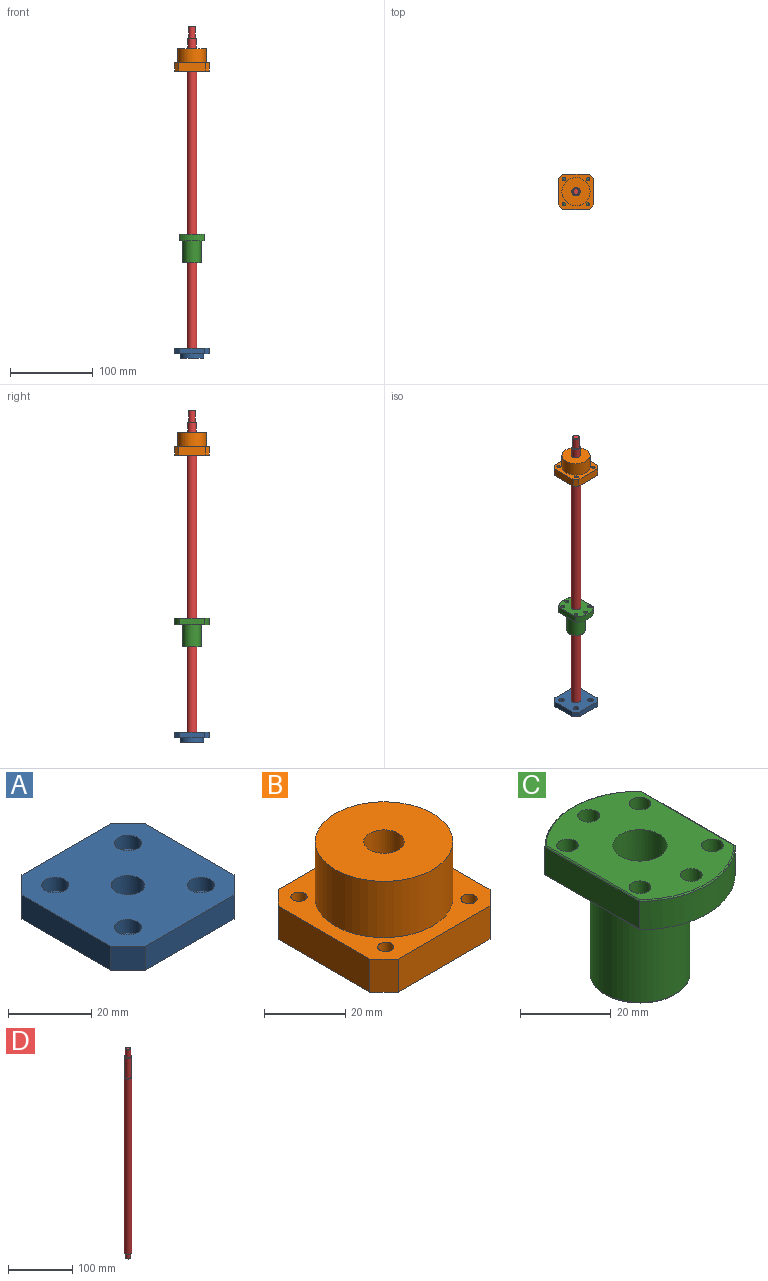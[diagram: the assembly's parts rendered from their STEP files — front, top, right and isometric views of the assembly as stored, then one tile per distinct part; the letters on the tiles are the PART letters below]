
ASSEMBLY  parts=4 mates=3
PART A: 25 faces, bbox 42x42x12 mm
  f0: cylinder r=2mm len=4mm, axis (0,0,-1), area 37.7mm2, adj f9,f23
  f1: cylinder r=2mm len=4mm, axis (0,0,-1), area 37.7mm2, adj f9,f21
  f2: cylinder r=2mm len=4mm, axis (0,0,-1), area 37.7mm2, adj f9,f19
  f3: cylinder r=2mm len=4mm, axis (0,0,-1), area 37.7mm2, adj f9,f17
  f4: plane 30x7mm, normal (0,-1,0), area 210mm2, adj f9,f10,f15,f16
  f5: plane 30x7mm, normal (1,0,0), area 210mm2, adj f9,f10,f14,f15
  f6: plane 30x7mm, normal (0,1,0), area 210mm2, adj f9,f10,f13,f14
  f7: cylinder r=4mm len=12mm, axis (0,0,1), area 301.6mm2, adj f10,f12
  f8: plane 30x7mm, normal (-1,0,0), area 210mm2, adj f9,f10,f13,f16
  f9: plane 42x42mm, normal (0,0,-1), area 1026mm2, adj f0,f1,f2,f3,f4,f5,f6,f8
  f10: plane 42x42mm, normal (0,0,1), area 1509mm2, adj f4,f5,f6,f7,f8,f13,f14,f15
  f11: cylinder r=14mm len=28mm, axis (0,0,1), area 439.8mm2, adj f9,f12
  f12: plane 28x28mm, normal (0,0,-1), area 565.5mm2, adj f7,f11
  f13: plane 7x6mm, normal (-0.71,0.71,0), area 59.4mm2, adj f6,f8,f9,f10
  f14: plane 7x6mm, normal (0.71,0.71,0), area 59.4mm2, adj f5,f6,f9,f10
  f15: plane 7x6mm, normal (0.71,-0.71,0), area 59.4mm2, adj f4,f5,f9,f10
  f16: plane 7x6mm, normal (-0.71,-0.71,0), area 59.4mm2, adj f4,f8,f9,f10
  f17: plane 6.5x6.5mm, normal (0,0,1), area 20.6mm2, adj f3,f18
  f18: cylinder r=3.25mm len=6.5mm, axis (0,0,1), area 81.7mm2, adj f10,f17
  f19: plane 6.5x6.5mm, normal (0,0,1), area 20.6mm2, adj f2,f20
  f20: cylinder r=3.25mm len=6.5mm, axis (0,0,1), area 81.7mm2, adj f10,f19
  f21: plane 6.5x6.5mm, normal (0,0,1), area 20.6mm2, adj f1,f22
  f22: cylinder r=3.25mm len=6.5mm, axis (0,0,1), area 81.7mm2, adj f10,f21
  f23: plane 6.5x6.5mm, normal (0,0,1), area 20.6mm2, adj f0,f24
  f24: cylinder r=3.25mm len=6.5mm, axis (0,0,1), area 81.7mm2, adj f10,f23
PART B: 25 faces, bbox 42x42x27 mm
  f0: cylinder r=2mm len=4mm, axis (0,0,1), area 50.3mm2, adj f8,f22
  f1: cylinder r=2mm len=4mm, axis (0,0,1), area 50.3mm2, adj f8,f20
  f2: cylinder r=2mm len=4mm, axis (0,0,1), area 50.3mm2, adj f8,f18
  f3: cylinder r=2mm len=4mm, axis (0,0,1), area 50.3mm2, adj f8,f16
  f4: plane 32x10mm, normal (1,0,0), area 320mm2, adj f8,f9,f13,f15
  f5: plane 32x10mm, normal (0,1,0), area 320mm2, adj f8,f9,f14,f15
  f6: plane 32x10mm, normal (-1,0,0), area 320mm2, adj f8,f9,f12,f14
  f7: plane 32x10mm, normal (0,-1,0), area 320mm2, adj f8,f9,f12,f13
  f8: plane 42x42mm, normal (0,0,1), area 755.8mm2, adj f0,f1,f2,f3,f4,f5,f6,f7
  f9: plane 42x42mm, normal (0,0,-1), area 1434.4mm2, adj f4,f5,f6,f7,f12,f13,f14,f15
  f10: cylinder r=17mm len=34mm, axis (0,0,-1), area 1815.8mm2, adj f8,f11
  f11: plane 34x34mm, normal (0,0,1), area 829.4mm2, adj f10,f24
  f12: plane 10x5mm, normal (-0.71,-0.71,0), area 70.7mm2, adj f6,f7,f8,f9
  f13: plane 10x5mm, normal (0.71,-0.71,0), area 70.7mm2, adj f4,f7,f8,f9
  f14: plane 10x5mm, normal (-0.71,0.71,0), area 70.7mm2, adj f5,f6,f8,f9
  f15: plane 10x5mm, normal (0.71,0.71,0), area 70.7mm2, adj f4,f5,f8,f9
  f16: plane 8x8mm, normal (0,0,-1), area 37.7mm2, adj f3,f17
  f17: cylinder r=4mm len=8mm, axis (0,0,-1), area 150.8mm2, adj f9,f16
  f18: plane 8x8mm, normal (0,0,-1), area 37.7mm2, adj f2,f19
  f19: cylinder r=4mm len=8mm, axis (0,0,-1), area 150.8mm2, adj f9,f18
  f20: plane 8x8mm, normal (0,0,-1), area 37.7mm2, adj f1,f21
  f21: cylinder r=4mm len=8mm, axis (0,0,-1), area 150.8mm2, adj f9,f20
  f22: plane 8x8mm, normal (0,0,-1), area 37.7mm2, adj f0,f23
  f23: cylinder r=4mm len=8mm, axis (0,0,-1), area 150.8mm2, adj f9,f22
  f24: cylinder r=5mm len=27mm, axis (0,0,1), area 848.2mm2, adj f9,f11
PART C: 23 faces, bbox 32.5x45.5x35 mm
  f0: cylinder r=11mm len=26.7mm, axis (0,0,1), area 1845.4mm2, adj f6,f21
  f1: plane 21.4x21.4mm, normal (0,0,-1), area 246.6mm2, adj f21,f22
  f2: plane 29.39x7.4mm, normal (1,0,0), area 217.5mm2, adj f3,f5,f14,f18
  f3: cylinder r=21mm len=30mm, axis (0,0,1), area 247.3mm2, adj f2,f4,f16,f19
  f4: plane 29.39x7.4mm, normal (-1,0,0), area 217.5mm2, adj f3,f5,f17,f20
  f5: cylinder r=21mm len=30mm, axis (0,0,1), area 257.2mm2, adj f2,f4,f6,f15,f18,f20
  f6: plane 41.7x29.4mm, normal (0,0,-1), area 626.3mm2, adj f0,f5,f8,f9,f10,f11,f12,f13
  f7: plane 41.4x29.4mm, normal (0,0,1), area 883.6mm2, adj f8,f9,f10,f11,f12,f13,f14,f15
  f8: cylinder r=2.4mm len=8mm, axis (0,0,1), area 120.6mm2, adj f6,f7
  f9: cylinder r=2.4mm len=8mm, axis (0,0,1), area 120.6mm2, adj f6,f7
  f10: cylinder r=2.4mm len=8mm, axis (0,0,1), area 120.6mm2, adj f6,f7
  f11: cylinder r=2.4mm len=8mm, axis (0,0,1), area 120.6mm2, adj f6,f7
  f12: cylinder r=2.4mm len=8mm, axis (0,0,1), area 120.6mm2, adj f6,f7
  f13: cylinder r=2.4mm len=8mm, axis (0,0,1), area 120.6mm2, adj f6,f7
  f14: cylinder r=0.3mm len=29.39mm, axis (0,1,0), area 13.8mm2, adj f2,f7,f15,f16
  f15: torus R=20.7mm, axis (0,0,1), area 15.6mm2, adj f5,f7,f14,f17
  f16: torus R=20.7mm, axis (0,0,1), area 15.6mm2, adj f3,f7,f14,f17
  f17: cylinder r=0.3mm len=29.39mm, axis (0,-1,0), area 13.8mm2, adj f4,f7,f15,f16
  f18: cylinder r=0.3mm len=29.69mm, axis (0,-1,0), area 13.9mm2, adj f2,f5,f6,f19
  f19: torus R=20.7mm, axis (0,0,1), area 15.6mm2, adj f3,f6,f18,f20
  f20: cylinder r=0.3mm len=29.69mm, axis (0,1,0), area 13.9mm2, adj f4,f5,f6,f19
  f21: torus R=10.7mm, axis (0,0,1), area 32.2mm2, adj f0,f1
  f22: cylinder r=6mm len=35mm, axis (0,0,-1), area 1319.5mm2, adj f1,f7
PART D: 14 faces, bbox 12x12x400 mm
  f0: cylinder r=5mm len=38.5mm, axis (0,0,1), area 1209.5mm2, adj f4,f12
  f1: plane 9x9mm, normal (0,0,1), area 13.4mm2, adj f3,f12
  f2: plane 7x7mm, normal (0,0,1), area 38.5mm2, adj f13
  f3: cylinder r=4mm len=14.5mm, axis (0,0,-1), area 364.4mm2, adj f1,f13
  f4: plane 11x11mm, normal (0,0,1), area 16.5mm2, adj f0,f11
  f5: cylinder r=6mm len=335mm, axis (0,0,-1), area 12629.2mm2, adj f10,f11
  f6: plane 11x11mm, normal (0,0,-1), area 44.8mm2, adj f8,f10
  f7: plane 7x7mm, normal (0,0,-1), area 38.5mm2, adj f9
  f8: cylinder r=4mm len=9.5mm, axis (0,0,-1), area 238.8mm2, adj f6,f9
  f9: cone r=4mm half-angle=45deg, axis (0,0,1), area 16.7mm2, adj f7,f8
  f10: cone r=6mm half-angle=45deg, axis (0,0,1), area 25.5mm2, adj f5,f6
  f11: cone r=5.5mm half-angle=45deg, axis (0,0,-1), area 25.5mm2, adj f4,f5
  f12: cone r=4.5mm half-angle=45deg, axis (0,0,-1), area 21.1mm2, adj f0,f1
  f13: cone r=3.5mm half-angle=45deg, axis (0,0,-1), area 16.7mm2, adj f2,f3
PLACE A rot(axis=(0,0,1),0deg) t=(265.21,-246.31,-46.76)mm
PLACE B rot(axis=(0,0,1),0deg) t=(265.21,-246.31,-47.76)mm
PLACE C rot(axis=(0,0,1),0deg) t=(265.21,-246.31,-58.85)mm
PLACE D rot(axis=(0,0,1),0deg) t=(265.21,-246.31,-47.26)mm
MATE slider D.f5 <-> C.f22  axis (0,0,-1) through (265.21,-246.31,130.74)mm
MATE fastened A.f7 <-> D.f5  axis (0,0,1) through (265.21,-246.31,-36.76)mm
MATE fastened B.f24 <-> D.f5  axis (0,0,-1) through (265.21,-246.31,298.24)mm
